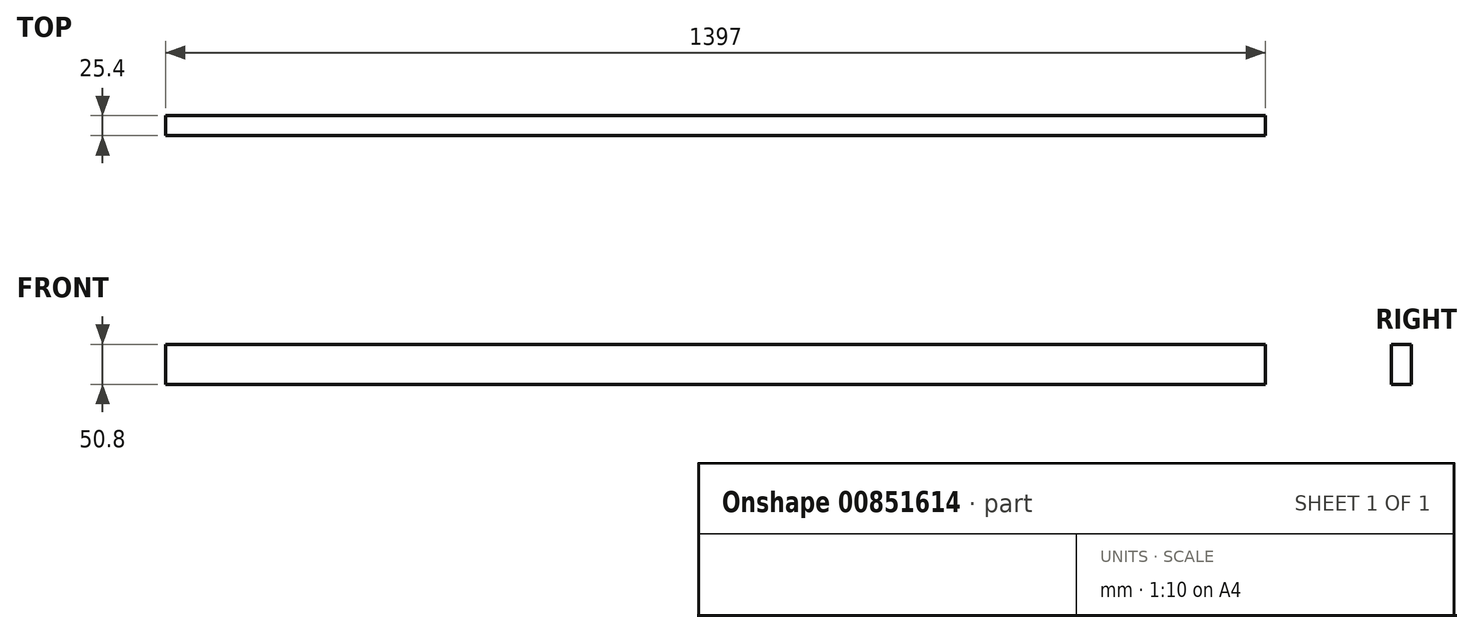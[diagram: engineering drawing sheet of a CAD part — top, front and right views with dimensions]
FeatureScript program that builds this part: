
annotation { "Feature Type Name" : "Feature", "Feature Type Description" : "" }
export const myFeature = defineFeature(function(context is Context, id is Id, definition is map)
    precondition{}
    {
        {
            var Q0;
            Q0=qCreatedBy(makeId("Front.planeOp"),FACE);
            var sketch = newSketch(context, id + "F0", { "sketchPlane" : qUnion([Q0])});
            skLineSegment(sketch, "E0", {"start": v(-290.84, -57.7) * mm, "end": v(-290.84, -108.5) * mm});
            skLineSegment(sketch, "E1", {"start": v(-290.84, -108.5) * mm, "end": v(1106.16, -108.5) * mm});
            skLineSegment(sketch, "E2", {"start": v(-290.84, -57.7) * mm, "end": v(1106.16, -57.7) * mm});
            skLineSegment(sketch, "E3", {"start": v(1106.16, -57.7) * mm, "end": v(1106.16, -108.5) * mm});
            skSolve(sketch);
        }
        {
            var Q0;
            Q0 = qSketchRegion(id + "F0", true);
            extrude(context, id + "F1", {"entities" : qUnion([Q0]), "depth" : 25.4 * mm, "offsetDistance" : 25.4 * mm});
        }
    });
